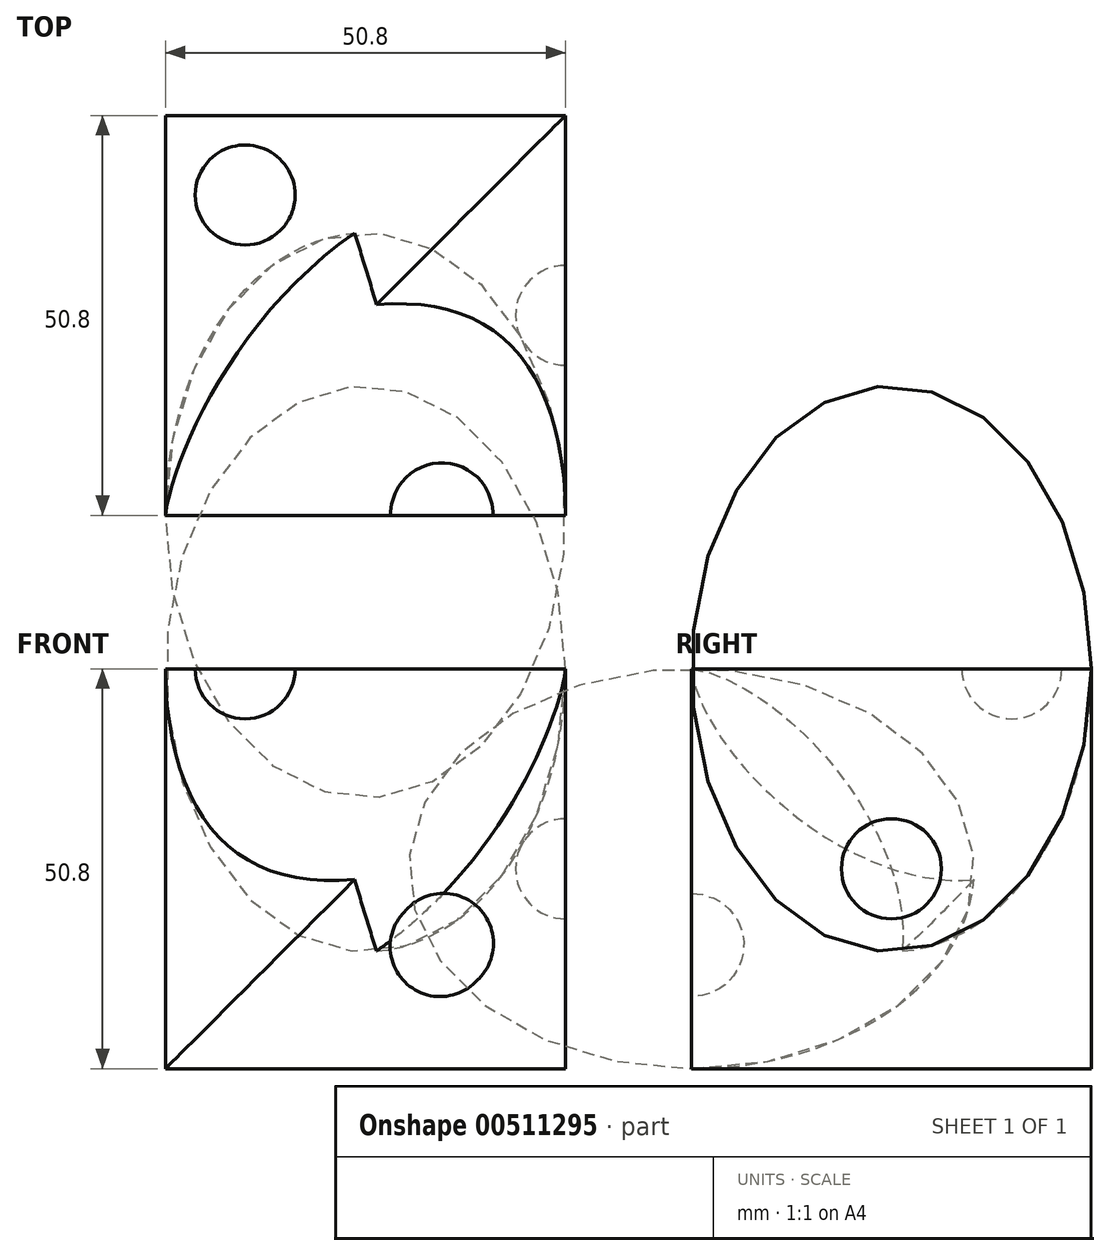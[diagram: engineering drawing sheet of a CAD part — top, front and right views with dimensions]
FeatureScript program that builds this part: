
annotation { "Feature Type Name" : "Feature", "Feature Type Description" : "" }
export const myFeature = defineFeature(function(context is Context, id is Id, definition is map)
    precondition{}
    {
        {
            var Q0;
            Q0=qCreatedBy(makeId("Front.planeOp"),FACE);
            var sketch = newSketch(context, id + "F0", { "sketchPlane" : qUnion([Q0])});
            skLineSegment(sketch, "E0", {"start": v(0, 0) * mm, "end": v(-50.8, 0) * mm});
            skLineSegment(sketch, "E1", {"start": v(-50.8, 0) * mm, "end": v(-50.8, 50.8) * mm});
            skLineSegment(sketch, "E2", {"start": v(-50.8, 50.8) * mm, "end": v(0, 50.8) * mm});
            skLineSegment(sketch, "E3", {"start": v(0, 50.8) * mm, "end": v(0, 0) * mm});
            skSolve(sketch);
        }
        {
            var Q0;
            Q0=makeQuery(id+"F0.imprint","IMPRINT",FACE,{"disambiguationData":[TD([[makeQuery(id+"F0.imprint","IMPRINT",EDGE,{"derivedFrom":sQuery(id+"F0.wireOp",EDGE,"E0")}),-1.0]])]});
            extrude(context, id + "F1", {"entities" : qUnion([Q0]), "depth" : 50.8 * mm, "offsetDistance" : 25.4 * mm});
        }
        {
            var Q0;
            Q0=makeQuery(id+"F1.opExtrude","SWEPT_FACE",FACE,{"disambiguationData":[OSD([sQuery(id+"F0.wireOp",EDGE,"E3")])]});
            var sketch = newSketch(context, id + "F2", { "sketchPlane" : qUnion([Q0])});
            skCircle(sketch, "E4", {"center": v(-25.4, 25.4) * mm, "radius": 6.35 * mm});
            skPoint(sketch, "E5.orphan", {"position": v(-50.8, 50.8) * mm});
            skPoint(sketch, "E6.orphan", {"position": v(0, 0) * mm});
            skLineSegment(sketch, "E7", {"start": v(-25.4, 50.8) * mm, "end": v(-25.4, 0) * mm});
            skSolve(sketch);
        }
        {
            var Q0;
            {var subQ0=sQuery(id+"F2.wireOp",EDGE,"E7");var subQ1=sQuery(id+"F2.wireOp",EDGE,"E4");var subQ2=makeQuery(id+"F2.imprint","INTERSECT",VERTEX,{"disambiguationData":[OD(0.0)],"derivedFrom":[subQ1,subQ0]});Q0=makeQuery(id+"F2.imprint","IMPRINT",FACE,{"disambiguationData":[TD([[makeQuery(id+"F2.imprint","IMPRINT",EDGE,{"disambiguationData":[TD([[subQ2,1.0]])],"derivedFrom":subQ1}),1.0]])]});}
            var Q1;
            Q1=sQuery(id+"F2.wireOp",EDGE,"E7");
            revolve(context, id + "F3", {"operationType" : NewBodyOperationType.REMOVE, "entities" : qUnion([Q0]), "axis" : qUnion([Q1]), "revolveType" : RevolveType.FULL});
        }
        {
            var Q0;
            Q0=makeQuery(id+"F1.opExtrude","CAP_FACE",FACE,{"disambiguationData":[OSD([sQuery(id+"F0.wireOp",EDGE,"E0"),sQuery(id+"F0.wireOp",EDGE,"E1"),sQuery(id+"F0.wireOp",EDGE,"E2"),sQuery(id+"F0.wireOp",EDGE,"E3")])],"isStart":false});
            var sketch = newSketch(context, id + "F4", { "sketchPlane" : qUnion([Q0])});
            skLineSegment(sketch, "E8", {"start": v(-50.8, 50.8) * mm, "end": v(0, 0) * mm});
            skCircle(sketch, "E9", {"center": v(-35.08, 35.08) * mm, "radius": 6.35 * mm});
            skCircle(sketch, "E10", {"center": v(-15.5, 15.92) * mm, "radius": 6.35 * mm});
            skSolve(sketch);
        }
        {
            var Q0;
            {var subQ0=sQuery(id+"F4.wireOp",EDGE,"E9");var subQ1=sQuery(id+"F4.wireOp",EDGE,"E8");var subQ2=makeQuery(id+"F4.imprint","INTERSECT",VERTEX,{"disambiguationData":[OD(0.0)],"derivedFrom":[subQ1,subQ0]});Q0=makeQuery(id+"F4.imprint","IMPRINT",FACE,{"disambiguationData":[TD([[makeQuery(id+"F4.imprint","IMPRINT",EDGE,{"disambiguationData":[TD([[subQ2,-1.0]])],"derivedFrom":subQ1}),1.0]])]});}
            var Q1;
            {var subQ0=sQuery(id+"F4.wireOp",EDGE,"E10");var subQ1=sQuery(id+"F4.wireOp",EDGE,"E8");var subQ2=makeQuery(id+"F4.imprint","INTERSECT",VERTEX,{"disambiguationData":[OD(0.0)],"derivedFrom":[subQ1,subQ0]});Q1=makeQuery(id+"F4.imprint","IMPRINT",FACE,{"disambiguationData":[TD([[makeQuery(id+"F4.imprint","IMPRINT",EDGE,{"disambiguationData":[TD([[subQ2,-1.0]])],"derivedFrom":subQ1}),1.0]])]});}
            var Q2;
            Q2=sQuery(id+"F4.wireOp",EDGE,"E8");
            revolve(context, id + "F5", {"operationType" : NewBodyOperationType.REMOVE, "entities" : qUnion([Q0, Q1]), "axis" : qUnion([Q2]), "revolveType" : RevolveType.FULL, "oppositeDirection" : true});
        }
        {
            var Q0;
            {var subQ0=sQuery(id+"F2.wireOp",EDGE,"E7");var subQ1=sQuery(id+"F2.wireOp",EDGE,"E4");var subQ2=makeQuery(id+"F2.imprint","INTERSECT",VERTEX,{"disambiguationData":[OD(0.0)],"derivedFrom":[subQ1,subQ0]});Q0=makeQuery(id+"F2.imprint","IMPRINT",FACE,{"disambiguationData":[TD([[makeQuery(id+"F2.imprint","IMPRINT",EDGE,{"disambiguationData":[TD([[subQ2,1.0]])],"derivedFrom":subQ1}),1.0]])]});}
            var Q1;
            Q1=sQuery(id+"F2.wireOp",EDGE,"E7");
            revolve(context, id + "F6", {"operationType" : NewBodyOperationType.REMOVE, "entities" : qUnion([Q0]), "axis" : qUnion([Q1]), "revolveType" : RevolveType.FULL, "oppositeDirection" : true});
        }
        {
            var Q0;
            Q0=makeQuery(id+"F1.opExtrude","SWEPT_FACE",FACE,{"disambiguationData":[OSD([sQuery(id+"F0.wireOp",EDGE,"E2")])]});
            var sketch = newSketch(context, id + "F7", { "sketchPlane" : qUnion([Q0])});
            skLineSegment(sketch, "E11", {"start": v(-50.8, 0) * mm, "end": v(0, -50.8) * mm});
            skCircle(sketch, "E12", {"center": v(-40.7, -10.1) * mm, "radius": 6.35 * mm});
            skCircle(sketch, "E13", {"center": v(-11.22, -39.58) * mm, "radius": 6.35 * mm});
            skCircle(sketch, "E14", {"center": v(-25.4, -25.4) * mm, "radius": 6.35 * mm});
            skSolve(sketch);
        }
        {
            var Q0;
            {var subQ0=sQuery(id+"F7.wireOp",EDGE,"E12");var subQ1=sQuery(id+"F7.wireOp",EDGE,"E11");var subQ2=makeQuery(id+"F7.imprint","INTERSECT",VERTEX,{"disambiguationData":[OD(0.0)],"derivedFrom":[subQ1,subQ0]});Q0=makeQuery(id+"F7.imprint","IMPRINT",FACE,{"disambiguationData":[TD([[makeQuery(id+"F7.imprint","IMPRINT",EDGE,{"disambiguationData":[TD([[subQ2,-1.0]])],"derivedFrom":subQ1}),-1.0]])]});}
            var Q1;
            {var subQ0=sQuery(id+"F7.wireOp",EDGE,"E14");var subQ1=sQuery(id+"F7.wireOp",EDGE,"E11");var subQ2=makeQuery(id+"F7.imprint","INTERSECT",VERTEX,{"disambiguationData":[OD(0.0)],"derivedFrom":[subQ1,subQ0]});Q1=makeQuery(id+"F7.imprint","IMPRINT",FACE,{"disambiguationData":[TD([[makeQuery(id+"F7.imprint","IMPRINT",EDGE,{"disambiguationData":[TD([[subQ2,-1.0]])],"derivedFrom":subQ1}),-1.0]])]});}
            var Q2;
            {var subQ0=sQuery(id+"F7.wireOp",EDGE,"E13");var subQ1=sQuery(id+"F7.wireOp",EDGE,"E11");var subQ2=makeQuery(id+"F7.imprint","INTERSECT",VERTEX,{"disambiguationData":[OD(0.0)],"derivedFrom":[subQ1,subQ0]});Q2=makeQuery(id+"F7.imprint","IMPRINT",FACE,{"disambiguationData":[TD([[makeQuery(id+"F7.imprint","IMPRINT",EDGE,{"disambiguationData":[TD([[subQ2,-1.0]])],"derivedFrom":subQ1}),-1.0]])]});}
            var Q3;
            Q3=sQuery(id+"F7.wireOp",EDGE,"E11");
            revolve(context, id + "F8", {"operationType" : NewBodyOperationType.REMOVE, "entities" : qUnion([Q0, Q1, Q2]), "axis" : qUnion([Q3]), "revolveType" : RevolveType.FULL, "oppositeDirection" : true});
        }
    });
